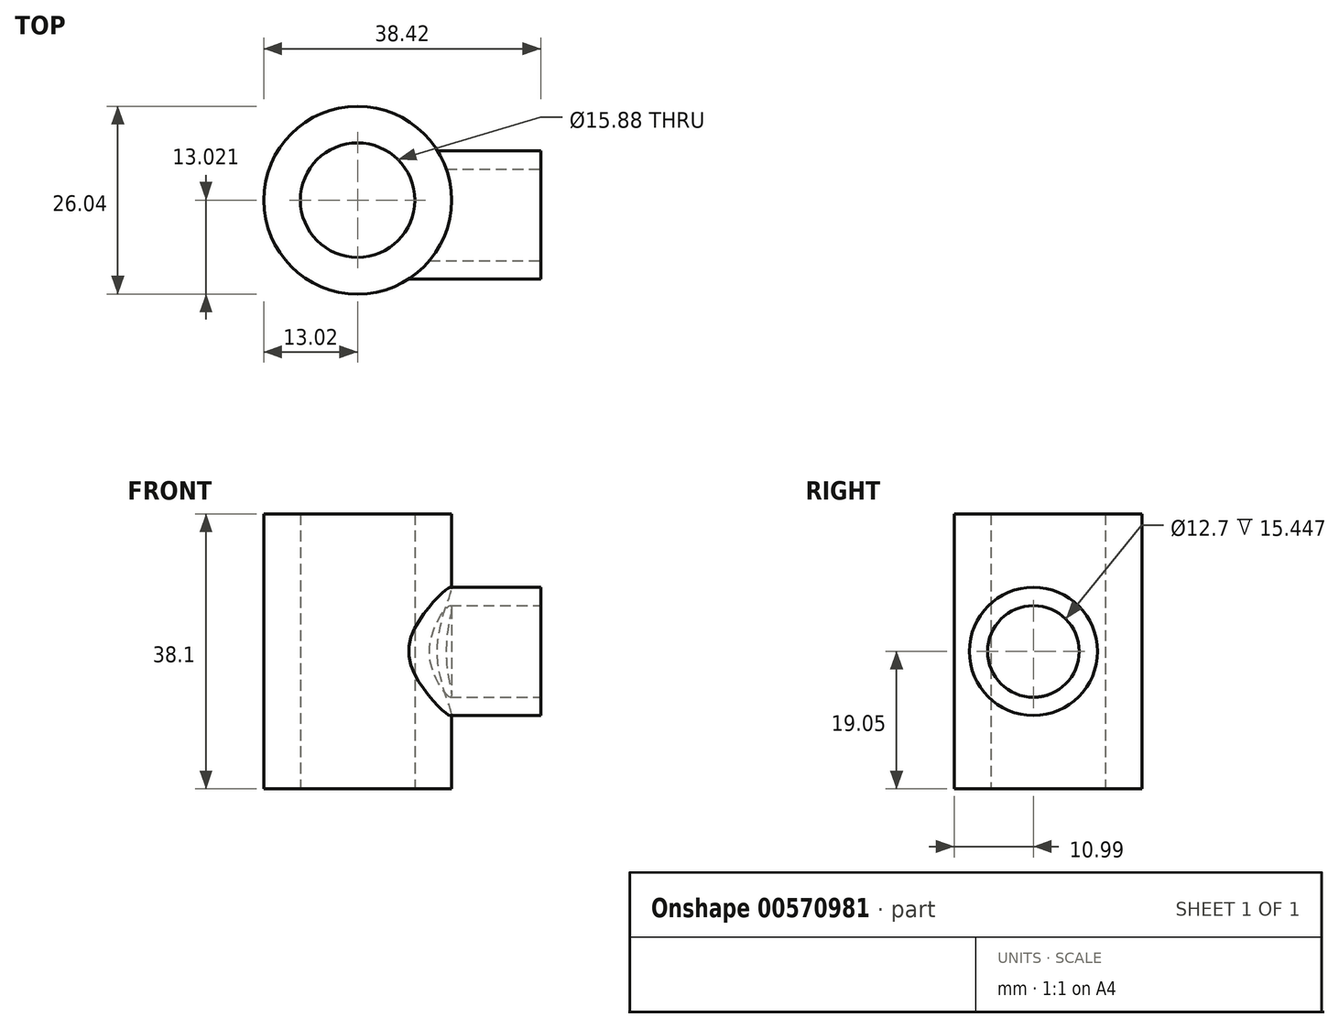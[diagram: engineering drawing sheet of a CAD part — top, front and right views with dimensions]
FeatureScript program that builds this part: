
annotation { "Feature Type Name" : "Feature", "Feature Type Description" : "" }
export const myFeature = defineFeature(function(context is Context, id is Id, definition is map)
    precondition{}
    {
        {
            var Q0;
            Q0=qCreatedBy(makeId("Top.planeOp"),FACE);
            var sketch = newSketch(context, id + "F0", { "sketchPlane" : qUnion([Q0])});
            skCircle(sketch, "E0", {"center": v(0, 2.03) * mm, "radius": 7.94 * mm});
            skCircle(sketch, "E1", {"center": v(0, 2.03) * mm, "radius": 13.02 * mm});
            skSolve(sketch);
        }
        {
            var Q0;
            Q0 = qSketchRegion(id + "F0", true);
            extrude(context, id + "F1", {"entities" : qUnion([Q0]), "depth" : 19.05 * mm, "offsetDistance" : 25.4 * mm, "hasSecondDirection" : true, "secondDirectionOppositeDirection" : true, "secondDirectionDepth" : 19.05 * mm});
        }
        {
            var Q0;
            Q0=qCreatedBy(makeId("Right.planeOp"),FACE);
            cPlane(context, id + "F2", {"entities" : qUnion([Q0]), "cplaneType" : CPlaneType.OFFSET, "offset" : 25.4 * mm, "width" : 152.4 * mm, "height" : 152.4 * mm});
        }
        {
            var Q0;
            Q0=qCreatedBy(id+"F2.planeOp",FACE);
            var sketch = newSketch(context, id + "F3", { "sketchPlane" : qUnion([Q0])});
            skCircle(sketch, "E2", {"center": v(0, 0) * mm, "radius": 6.35 * mm});
            skCircle(sketch, "E3", {"center": v(0, 0) * mm, "radius": 8.9 * mm});
            skSolve(sketch);
        }
        {
            var Q0;
            Q0 = qSketchRegion(id + "F3", true);
            var Q1;
            Q1=makeQuery(id+"F1.opExtrude","SWEPT_FACE",FACE,{"disambiguationData":[OSD([sQuery(id+"F0.wireOp",EDGE,"E1")])]});
            extrude(context, id + "F4", {"entities" : qUnion([Q0]), "operationType" : NewBodyOperationType.ADD, "endBound" : BoundingType.UP_TO_SURFACE, "oppositeDirection" : true, "depth" : 25.4 * mm, "endBoundEntityFace" : qUnion([Q1]), "offsetDistance" : 25.4 * mm});
        }
    });
